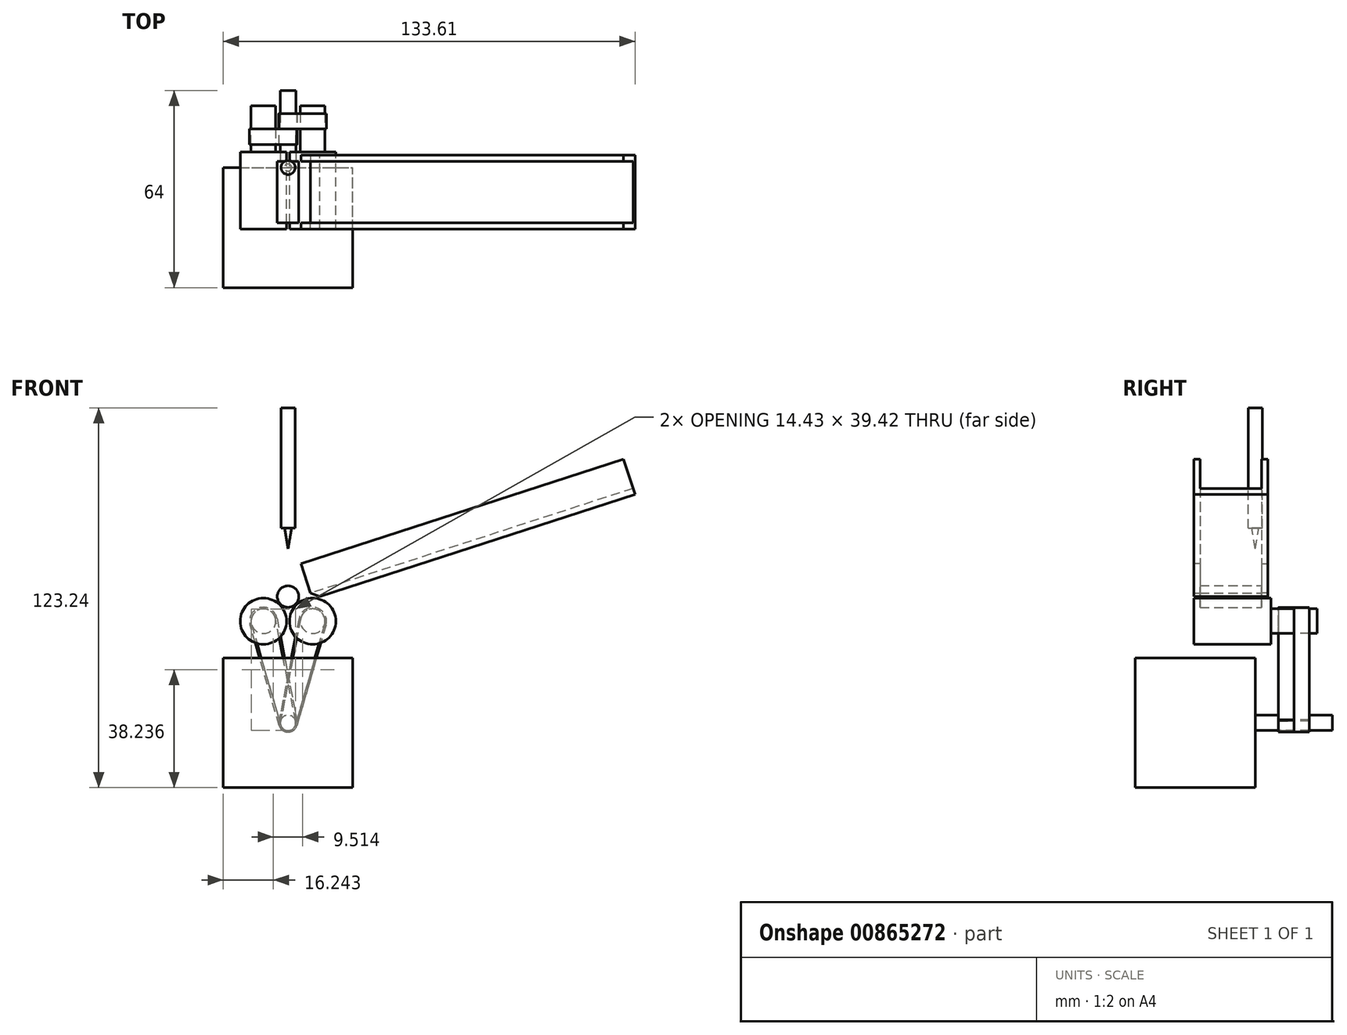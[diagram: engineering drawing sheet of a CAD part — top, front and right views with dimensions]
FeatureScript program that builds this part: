
annotation { "Feature Type Name" : "Feature", "Feature Type Description" : "" }
export const myFeature = defineFeature(function(context is Context, id is Id, definition is map)
    precondition{}
    {
        {
            var Q0;
            Q0=qCreatedBy(makeId("Front.planeOp"),FACE);
            var sketch = newSketch(context, id + "F0", { "sketchPlane" : qUnion([Q0])});
            skCircle(sketch, "E0", {"center": v(-8, -8) * mm, "radius": 7.5 * mm});
            skCircle(sketch, "E1", {"center": v(8, -8) * mm, "radius": 7.5 * mm});
            skCircle(sketch, "E2", {"center": v(0, 0) * mm, "radius": 3.5 * mm});
            skLineSegment(sketch, "E3.bottom", {"start": v(-21, -20) * mm, "end": v(21, -20) * mm});
            skLineSegment(sketch, "E3.top", {"start": v(-21, -62) * mm, "end": v(21, -62) * mm});
            skLineSegment(sketch, "E3.left", {"start": v(-21, -20) * mm, "end": v(-21, -62) * mm});
            skLineSegment(sketch, "E3.right", {"start": v(21, -20) * mm, "end": v(21, -62) * mm});
            skCircle(sketch, "E4", {"center": v(0, -41) * mm, "radius": 2.5 * mm});
            skSolve(sketch);
        }
        {
            var Q0;
            Q0=makeQuery(id+"F0.imprint","IMPRINT",FACE,{"disambiguationData":[TD([[makeQuery(id+"F0.imprint","IMPRINT",EDGE,{"derivedFrom":sQuery(id+"F0.wireOp",EDGE,"E0")}),1.0]])]});
            var Q1;
            Q1=makeQuery(id+"F0.imprint","IMPRINT",FACE,{"disambiguationData":[TD([[makeQuery(id+"F0.imprint","IMPRINT",EDGE,{"derivedFrom":sQuery(id+"F0.wireOp",EDGE,"E1")}),1.0]])]});
            extrude(context, id + "F1", {"entities" : qUnion([Q0, Q1]), "depth" : 20 * mm, "offsetDistance" : 25 * mm, "hasSecondDirection" : true, "secondDirectionOppositeDirection" : true, "secondDirectionDepth" : 5 * mm});
        }
        {
            var Q0;
            Q0=makeQuery(id+"F0.imprint","IMPRINT",FACE,{"disambiguationData":[TD([[makeQuery(id+"F0.imprint","IMPRINT",EDGE,{"derivedFrom":sQuery(id+"F0.wireOp",EDGE,"E3.bottom")}),-1.0]])]});
            extrude(context, id + "F2", {"entities" : qUnion([Q0]), "depth" : 39 * mm, "offsetDistance" : 25 * mm});
        }
        {
            var Q0;
            Q0=makeQuery(id+"F0.imprint","IMPRINT",FACE,{"disambiguationData":[TD([[makeQuery(id+"F0.imprint","IMPRINT",EDGE,{"derivedFrom":sQuery(id+"F0.wireOp",EDGE,"E2")}),1.0]])]});
            extrude(context, id + "F3", {"entities" : qUnion([Q0]), "depth" : 18 * mm, "offsetDistance" : 25 * mm, "hasSecondDirection" : true, "secondDirectionOppositeDirection" : true, "secondDirectionDepth" : 2 * mm});
        }
        {
            var Q0;
            Q0=makeQuery(id+"F0.imprint","IMPRINT",FACE,{"disambiguationData":[TD([[makeQuery(id+"F0.imprint","IMPRINT",EDGE,{"derivedFrom":sQuery(id+"F0.wireOp",EDGE,"E4")}),1.0]])]});
            extrude(context, id + "F4", {"entities" : qUnion([Q0]), "operationType" : NewBodyOperationType.ADD, "depth" : 39 * mm, "offsetDistance" : 25 * mm});
        }
        {
            var Q0;
            Q0=makeQuery(id+"F0.imprint","IMPRINT",FACE,{"disambiguationData":[TD([[makeQuery(id+"F0.imprint","IMPRINT",EDGE,{"derivedFrom":sQuery(id+"F0.wireOp",EDGE,"E4")}),1.0]])]});
            extrude(context, id + "F5", {"entities" : qUnion([Q0]), "operationType" : NewBodyOperationType.ADD, "oppositeDirection" : true, "depth" : 25 * mm, "offsetDistance" : 25 * mm});
        }
        {
            var Q0;
            Q0=makeQuery(id+"F1.opExtrude","CAP_FACE",FACE,{"disambiguationData":[OSD([sQuery(id+"F0.wireOp",EDGE,"E1")])],"isStart":true});
            var sketch = newSketch(context, id + "F6", { "sketchPlane" : qUnion([Q0])});
            skCircle(sketch, "E5", {"center": v(-8, -8) * mm, "radius": 4 * mm});
            skCircle(sketch, "E6", {"center": v(8, -8) * mm, "radius": 4 * mm});
            skSolve(sketch);
        }
        {
            var Q0;
            Q0 = qSketchRegion(id + "F6", true);
            extrude(context, id + "F7", {"entities" : qUnion([Q0]), "operationType" : NewBodyOperationType.ADD, "depth" : 15 * mm, "offsetDistance" : 25 * mm});
        }
        {
            var Q0;
            Q0=makeQuery(id+"F7.opExtrude","CAP_FACE",FACE,{"disambiguationData":[OSD([sQuery(id+"F6.wireOp",EDGE,"E5")])],"isStart":false});
            cPlane(context, id + "F8", {"entities" : qUnion([Q0]), "cplaneType" : CPlaneType.OFFSET, "offset" : 7.5 * mm, "oppositeDirection" : true, "width" : 150 * mm, "height" : 150 * mm});
        }
        {
            var Q0;
            Q0=qCreatedBy(id+"F8.planeOp",FACE);
            var sketch = newSketch(context, id + "F9", { "sketchPlane" : qUnion([Q0])});
            skArc(sketch, "E7", {"start": v(-3.58, -7.13) * mm, "mid": v(-9.06, -3.63) * mm, "end": v(-12.32, -9.25) * mm});
            skArc(sketch, "E8", {"start": v(12.32, -9.25) * mm, "mid": v(9.06, -3.63) * mm, "end": v(3.58, -7.13) * mm});
            skArc(sketch, "E9", {"start": v(-2.86, -40.1) * mm, "mid": v(0, -44) * mm, "end": v(2.86, -40.1) * mm});
            skLineSegment(sketch, "E10", {"start": v(-12.32, -9.25) * mm, "end": v(-2.88, -41.83) * mm});
            skLineSegment(sketch, "E11", {"start": v(-3.58, -7.13) * mm, "end": v(2.94, -40.42) * mm});
            skLineSegment(sketch, "E12", {"start": v(2.88, -41.83) * mm, "end": v(12.32, -9.25) * mm});
            skLineSegment(sketch, "E13", {"start": v(3.58, -7.13) * mm, "end": v(-2.94, -40.42) * mm});
            skArc(sketch, "E14", {"start": v(-4.07, -7.23) * mm, "mid": v(-8.94, -4.11) * mm, "end": v(-11.84, -9.11) * mm});
            skArc(sketch, "E15", {"start": v(11.84, -9.11) * mm, "mid": v(8.94, -4.11) * mm, "end": v(4.07, -7.23) * mm});
            skArc(sketch, "E16", {"start": v(-2.45, -40.52) * mm, "mid": v(0, -43.5) * mm, "end": v(2.45, -40.52) * mm});
            skLineSegment(sketch, "E17", {"start": v(-11.84, -9.11) * mm, "end": v(-2.4, -41.7) * mm});
            skLineSegment(sketch, "E18", {"start": v(-4.07, -7.23) * mm, "end": v(2.45, -40.52) * mm});
            skLineSegment(sketch, "E19", {"start": v(11.84, -9.11) * mm, "end": v(2.36, -41.83) * mm});
            skLineSegment(sketch, "E20", {"start": v(-2.45, -40.52) * mm, "end": v(4.07, -7.23) * mm});
            skSolve(sketch);
        }
        {
            var Q0;
            {var subQ2=sQuery(id+"F9.wireOp",EDGE,"E7");Q0=makeQuery(id+"F9.imprint","IMPRINT",FACE,{"disambiguationData":[TD([[makeQuery(id+"F9.imprint","IMPRINT",EDGE,{"derivedFrom":subQ2}),1.0]])]});}
            var Q1;
            {var subQ0=sQuery(id+"F9.wireOp",EDGE,"E13");var subQ1=sQuery(id+"F9.wireOp",EDGE,"E11");var subQ2=makeQuery(id+"F9.imprint","INTERSECT",VERTEX,{"derivedFrom":[subQ1,subQ0]});Q1=makeQuery(id+"F9.imprint","IMPRINT",FACE,{"disambiguationData":[TD([[makeQuery(id+"F9.imprint","IMPRINT",EDGE,{"disambiguationData":[TD([[subQ2,-1.0]])],"derivedFrom":subQ1}),-1.0]])]});}
            var Q2;
            {var subQ2=sQuery(id+"F9.wireOp",EDGE,"E11");var subQ7=sQuery(id+"F9.wireOp",EDGE,"E20");var subQ10=makeQuery(id+"F9.imprint","INTERSECT",VERTEX,{"derivedFrom":[subQ2,subQ7]});Q2=makeQuery(id+"F9.imprint","IMPRINT",FACE,{"disambiguationData":[TD([[makeQuery(id+"F9.imprint","IMPRINT",EDGE,{"disambiguationData":[TD([[subQ10,-1.0]])],"derivedFrom":subQ2}),-1.0]])]});}
            var Q3;
            {var subQ0=sQuery(id+"F9.wireOp",EDGE,"E9");var subQ5=sQuery(id+"F9.wireOp",EDGE,"E17");var subQ6=makeQuery(id+"F9.imprint","INTERSECT",VERTEX,{"derivedFrom":[subQ0,subQ5]});Q3=makeQuery(id+"F9.imprint","IMPRINT",FACE,{"disambiguationData":[TD([[makeQuery(id+"F9.imprint","IMPRINT",EDGE,{"disambiguationData":[TD([[subQ6,-1.0]])],"derivedFrom":subQ0}),1.0]])]});}
            extrude(context, id + "F10", {"entities" : qUnion([Q0, Q1, Q2, Q3]), "depth" : 5 * mm, "offsetDistance" : 25 * mm});
        }
        {
            var Q0;
            {var subQ11=sQuery(id+"F9.wireOp",EDGE,"E8");Q0=makeQuery(id+"F9.imprint","IMPRINT",FACE,{"disambiguationData":[TD([[makeQuery(id+"F9.imprint","IMPRINT",EDGE,{"derivedFrom":subQ11}),1.0]])]});}
            var Q1;
            {var subQ0=sQuery(id+"F9.wireOp",EDGE,"E13");var subQ1=sQuery(id+"F9.wireOp",EDGE,"E11");var subQ2=makeQuery(id+"F9.imprint","INTERSECT",VERTEX,{"derivedFrom":[subQ1,subQ0]});Q1=makeQuery(id+"F9.imprint","IMPRINT",FACE,{"disambiguationData":[TD([[makeQuery(id+"F9.imprint","IMPRINT",EDGE,{"disambiguationData":[TD([[subQ2,-1.0]])],"derivedFrom":subQ1}),-1.0]])]});}
            var Q2;
            {var subQ2=sQuery(id+"F9.wireOp",EDGE,"E13");var subQ8=sQuery(id+"F9.wireOp",EDGE,"E18");var subQ9=makeQuery(id+"F9.imprint","INTERSECT",VERTEX,{"derivedFrom":[subQ2,subQ8]});Q2=makeQuery(id+"F9.imprint","IMPRINT",FACE,{"disambiguationData":[TD([[makeQuery(id+"F9.imprint","IMPRINT",EDGE,{"disambiguationData":[TD([[subQ9,-1.0]])],"derivedFrom":subQ2}),1.0]])]});}
            var Q3;
            {var subQ0=sQuery(id+"F9.wireOp",EDGE,"E9");var subQ5=sQuery(id+"F9.wireOp",EDGE,"E17");var subQ6=makeQuery(id+"F9.imprint","INTERSECT",VERTEX,{"derivedFrom":[subQ0,subQ5]});Q3=makeQuery(id+"F9.imprint","IMPRINT",FACE,{"disambiguationData":[TD([[makeQuery(id+"F9.imprint","IMPRINT",EDGE,{"disambiguationData":[TD([[subQ6,-1.0]])],"derivedFrom":subQ0}),1.0]])]});}
            extrude(context, id + "F11", {"entities" : qUnion([Q0, Q1, Q2, Q3]), "oppositeDirection" : true, "depth" : 5 * mm, "offsetDistance" : 25 * mm});
        }
        {
            var Q0;
            Q0=qCreatedBy(makeId("Front.planeOp"),FACE);
            var sketch = newSketch(context, id + "F12", { "sketchPlane" : qUnion([Q0])});
            skLineSegment(sketch, "E21", {"start": v(0, 67.2) * mm, "end": v(0, 11.8) * mm, "construction": true});
            skLineSegment(sketch, "E22", {"start": v(0, 61.24) * mm, "end": v(2.3, 61.24) * mm});
            skLineSegment(sketch, "E23", {"start": v(2.3, 61.24) * mm, "end": v(2.3, 22.18) * mm});
            skLineSegment(sketch, "E24", {"start": v(2.3, 22.18) * mm, "end": v(0, 22.18) * mm});
            skLineSegment(sketch, "E25", {"start": v(1.15, 22.18) * mm, "end": v(0, 15.48) * mm});
            skLineSegment(sketch, "E26", {"start": v(0, 61.24) * mm, "end": v(0, 15.48) * mm});
            skSolve(sketch);
        }
        {
            var Q0;
            {var subQ5=sQuery(id+"F12.wireOp",EDGE,"E22");Q0=makeQuery(id+"F12.imprint","IMPRINT",FACE,{"disambiguationData":[TD([[makeQuery(id+"F12.imprint","IMPRINT",EDGE,{"derivedFrom":subQ5}),-1.0]])]});}
            var Q1;
            Q1=sQuery(id+"F12.wireOp",EDGE,"E21");
            revolve(context, id + "F13", {"surfaceOperationType" : NewSurfaceOperationType.NEW, "entities" : qUnion([Q0]), "axis" : qUnion([Q1]), "revolveType" : RevolveType.FULL});
        }
        {
            var Q0;
            {var subQ3=sQuery(id+"F12.wireOp",EDGE,"E25");Q0=makeQuery(id+"F12.imprint","IMPRINT",FACE,{"disambiguationData":[TD([[makeQuery(id+"F12.imprint","IMPRINT",EDGE,{"derivedFrom":subQ3}),-1.0]])]});}
            var Q1;
            Q1=sQuery(id+"F12.wireOp",EDGE,"E21");
            revolve(context, id + "F14", {"surfaceOperationType" : NewSurfaceOperationType.NEW, "entities" : qUnion([Q0]), "axis" : qUnion([Q1]), "revolveType" : RevolveType.FULL});
        }
        {
            var Q0;
            Q0=qCreatedBy(makeId("Front.planeOp"),FACE);
            var sketch = newSketch(context, id + "F15", { "sketchPlane" : qUnion([Q0])});
            skLineSegment(sketch, "E27", {"start": v(10.35, 0) * mm, "end": v(112.61, 33.17) * mm});
            skLineSegment(sketch, "E28", {"start": v(112.61, 33.17) * mm, "end": v(112, 35.08) * mm});
            skLineSegment(sketch, "E29", {"start": v(112, 35.08) * mm, "end": v(7.27, 1.1) * mm});
            skLineSegment(sketch, "E30", {"start": v(7.27, 1.1) * mm, "end": v(10.35, 0) * mm});
            skSolve(sketch);
        }
        {
            var Q0;
            Q0 = qSketchRegion(id + "F15", true);
            var Q1;
            Q1=makeQuery(id+"F3.opExtrude","CAP_FACE",FACE,{"disambiguationData":[OSD([sQuery(id+"F0.wireOp",EDGE,"E2")])],"isStart":false});
            var Q2;
            Q2=makeQuery(id+"F3.opExtrude","CAP_FACE",FACE,{"disambiguationData":[OSD([sQuery(id+"F0.wireOp",EDGE,"E2")])],"isStart":true});
            extrude(context, id + "F16", {"entities" : qUnion([Q0]), "endBound" : BoundingType.UP_TO_SURFACE, "depth" : 25 * mm, "endBoundEntityFace" : qUnion([Q1]), "offsetDistance" : 25 * mm, "hasSecondDirection" : true, "secondDirectionBound" : SecondDirectionBoundingType.UP_TO_SURFACE, "secondDirectionOppositeDirection" : true, "secondDirectionDepth" : 25 * mm, "secondDirectionBoundEntityFace" : qUnion([Q2])});
        }
        {
            var Q0;
            Q0=makeQuery(id+"F16.opExtrude","SWEPT_FACE",FACE,{"disambiguationData":[OSD([sQuery(id+"F15.wireOp",EDGE,"E29")])]});
            var sketch = newSketch(context, id + "F17", { "sketchPlane" : qUnion([Q0])});
            skLineSegment(sketch, "E31.bottom", {"start": v(7.26, 2) * mm, "end": v(117.35, 2) * mm});
            skLineSegment(sketch, "E31.top", {"start": v(7.26, 4) * mm, "end": v(117.35, 4) * mm});
            skLineSegment(sketch, "E31.left", {"start": v(7.26, 2) * mm, "end": v(7.26, 4) * mm});
            skLineSegment(sketch, "E31.right", {"start": v(117.35, 2) * mm, "end": v(117.35, 4) * mm});
            skLineSegment(sketch, "E32.bottom", {"start": v(117.35, -18) * mm, "end": v(7.26, -18) * mm});
            skLineSegment(sketch, "E32.top", {"start": v(117.35, -20) * mm, "end": v(7.26, -20) * mm});
            skLineSegment(sketch, "E32.left", {"start": v(117.35, -18) * mm, "end": v(117.35, -20) * mm});
            skLineSegment(sketch, "E32.right", {"start": v(7.26, -18) * mm, "end": v(7.26, -20) * mm});
            skSolve(sketch);
        }
        {
            var Q0;
            Q0 = qSketchRegion(id + "F17", true);
            extrude(context, id + "F18", {"entities" : qUnion([Q0]), "operationType" : NewBodyOperationType.ADD, "depth" : 10 * mm, "offsetDistance" : 25 * mm, "hasSecondDirection" : true, "secondDirectionOppositeDirection" : true, "secondDirectionDepth" : 2 * mm});
        }
        {
            var Q0;
            {var subQ0=sQuery(id+"F17.wireOp",EDGE,"E32.bottom");var subQ1=makeQuery(id+"F18.opExtrude","SWEPT_FACE",FACE,{"disambiguationData":[OSD([subQ0])]});Q0=makeQuery(id+"F18.boolean.opBoolean","SPLIT",FACE,{"disambiguationData":[TD([makeQuery(id+"F16.opExtrude","SWEPT_FACE",FACE,{"disambiguationData":[OSD([sQuery(id+"F15.wireOp",EDGE,"E27")])]})])],"derivedFrom":subQ1});}
            extrude(context, id + "F19", {"entities" : qUnion([Q0]), "operationType" : NewBodyOperationType.REMOVE, "oppositeDirection" : true, "depth" : 25 * mm, "offsetDistance" : 25 * mm});
        }
        {
            var Q0;
            {var subQ0=sQuery(id+"F17.wireOp",EDGE,"E31.bottom");var subQ1=makeQuery(id+"F18.opExtrude","SWEPT_FACE",FACE,{"disambiguationData":[OSD([subQ0])]});Q0=makeQuery(id+"F18.boolean.opBoolean","SPLIT",FACE,{"disambiguationData":[TD([makeQuery(id+"F16.opExtrude","SWEPT_FACE",FACE,{"disambiguationData":[OSD([sQuery(id+"F15.wireOp",EDGE,"E27")])]})])],"derivedFrom":subQ1});}
            extrude(context, id + "F20", {"entities" : qUnion([Q0]), "operationType" : NewBodyOperationType.REMOVE, "oppositeDirection" : true, "depth" : 25 * mm, "offsetDistance" : 25 * mm});
        }
    });
